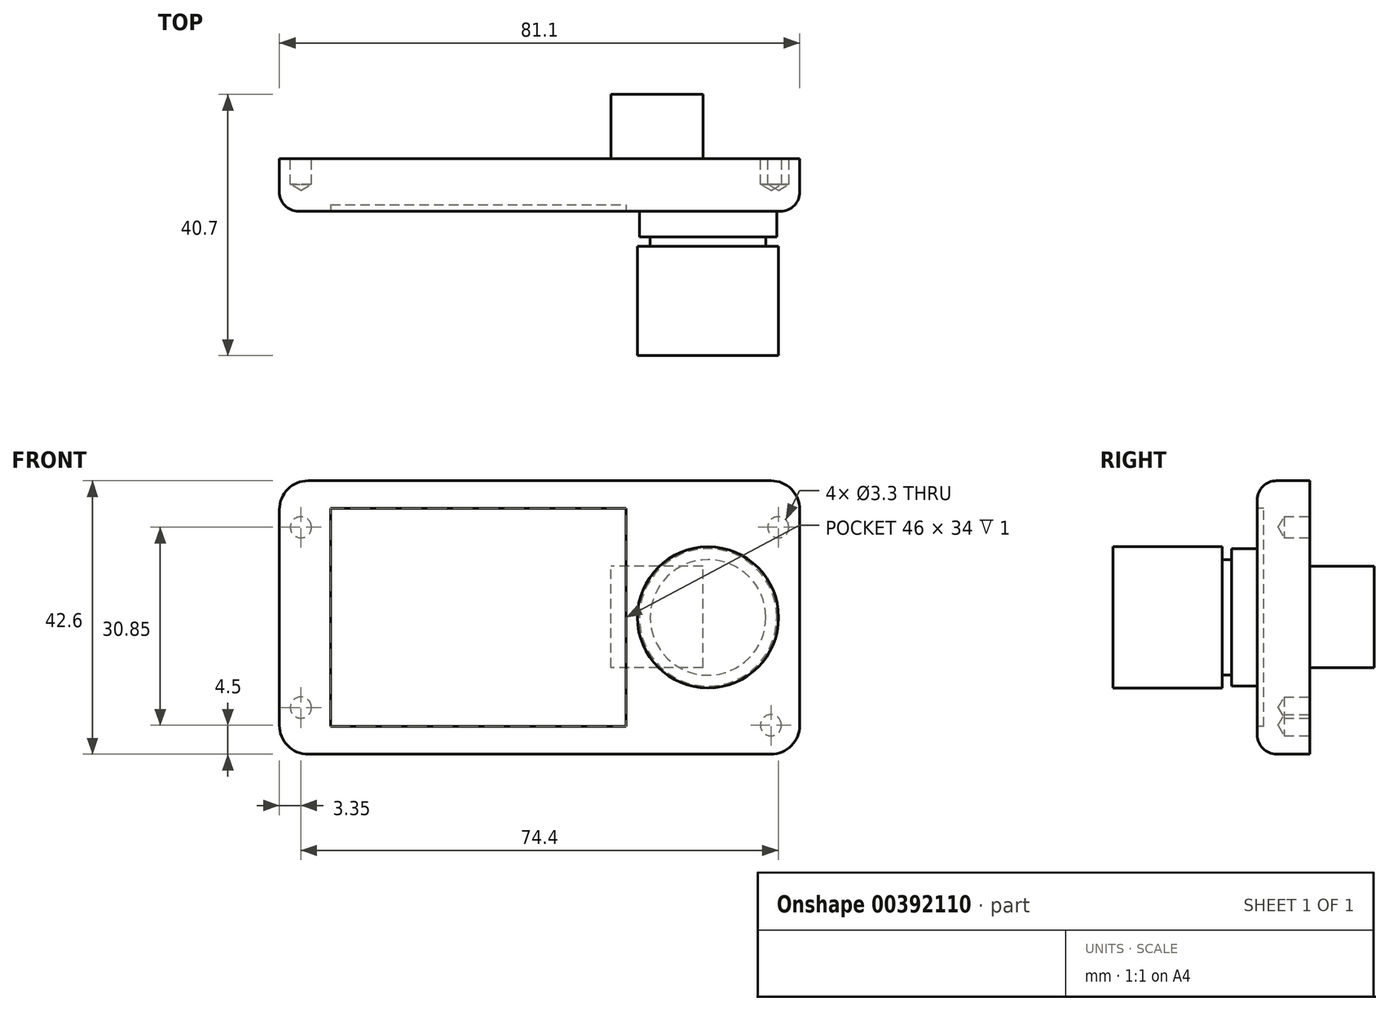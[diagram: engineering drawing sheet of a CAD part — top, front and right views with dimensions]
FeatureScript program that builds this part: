
annotation { "Feature Type Name" : "Feature", "Feature Type Description" : "" }
export const myFeature = defineFeature(function(context is Context, id is Id, definition is map)
    precondition{}
    {
        {
            var Q0;
            Q0=qCreatedBy(makeId("Front.planeOp"),FACE);
            var sketch = newSketch(context, id + "F0", { "sketchPlane" : qUnion([Q0])});
            skLineSegment(sketch, "E0.bottom", {"start": v(36.05, 21.3) * mm, "end": v(-36.05, 21.3) * mm});
            skLineSegment(sketch, "E0.top", {"start": v(36.05, -21.3) * mm, "end": v(-36.05, -21.3) * mm});
            skLineSegment(sketch, "E0.left", {"start": v(40.55, 16.8) * mm, "end": v(40.55, -16.8) * mm});
            skLineSegment(sketch, "E0.right", {"start": v(-40.55, 16.8) * mm, "end": v(-40.55, -16.8) * mm});
            skPoint(sketch, "E0.middle", {"position": v(0, 0) * mm});
            skArc(sketch, "E1.filletArc", {"start": v(-36.05, 21.3) * mm, "mid": v(-39.23, 19.98) * mm, "end": v(-40.55, 16.8) * mm});
            skPoint(sketch, "E2.visualSharp", {"position": v(40.55, 21.3) * mm});
            skArc(sketch, "E2.filletArc", {"start": v(40.55, 16.8) * mm, "mid": v(39.23, 19.98) * mm, "end": v(36.05, 21.3) * mm});
            skPoint(sketch, "E3.visualSharp", {"position": v(40.55, -21.3) * mm});
            skArc(sketch, "E3.filletArc", {"start": v(36.05, -21.3) * mm, "mid": v(39.23, -19.98) * mm, "end": v(40.55, -16.8) * mm});
            skPoint(sketch, "E4.visualSharp", {"position": v(-40.55, -21.3) * mm});
            skArc(sketch, "E4.filletArc", {"start": v(-40.55, -16.8) * mm, "mid": v(-39.23, -19.98) * mm, "end": v(-36.05, -21.3) * mm});
            skLineSegment(sketch, "E5", {"start": v(40.55, 0) * mm, "end": v(-40.55, 0) * mm, "construction": true});
            skLineSegment(sketch, "E6", {"start": v(0, 21.3) * mm, "end": v(0, -21.3) * mm, "construction": true});
            skLineSegment(sketch, "E7.bottom", {"start": v(-37.2, 14.05) * mm, "end": v(37.2, 14.05) * mm, "construction": true});
            skLineSegment(sketch, "E7.top", {"start": v(-37.2, -14.05) * mm, "end": v(37.2, -14.05) * mm, "construction": true});
            skLineSegment(sketch, "E7.left", {"start": v(-37.2, 14.05) * mm, "end": v(-37.2, -14.05) * mm, "construction": true});
            skLineSegment(sketch, "E7.right", {"start": v(37.2, 14.05) * mm, "end": v(37.2, -14.05) * mm, "construction": true});
            skPoint(sketch, "E8", {"position": v(37.2, 14.05) * mm});
            skPoint(sketch, "E9", {"position": v(37.2, -14.05) * mm});
            skPoint(sketch, "E10", {"position": v(-37.2, -14.05) * mm});
            skPoint(sketch, "E11", {"position": v(-37.2, 14.05) * mm});
            skSolve(sketch);
        }
        {
            var Q0;
            Q0=makeQuery(id+"F0.imprint","IMPRINT",FACE,{"disambiguationData":[TD([[makeQuery(id+"F0.imprint","IMPRINT",EDGE,{"derivedFrom":sQuery(id+"F0.wireOp",EDGE,"E0.bottom")}),1.0]])]});
            extrude(context, id + "F1", {"entities" : qUnion([Q0]), "depth" : 8.2 * mm});
        }
        {
            var Q0;
            Q0=makeQuery(id+"F1.opExtrude","CAP_FACE",FACE,{"disambiguationData":[OSD([sQuery(id+"F0.wireOp",EDGE,"E0.bottom"),sQuery(id+"F0.wireOp",EDGE,"E0.top"),sQuery(id+"F0.wireOp",EDGE,"E0.left"),sQuery(id+"F0.wireOp",EDGE,"E0.right"),sQuery(id+"F0.wireOp",EDGE,"E1.filletArc"),sQuery(id+"F0.wireOp",EDGE,"E2.filletArc"),sQuery(id+"F0.wireOp",EDGE,"E3.filletArc"),sQuery(id+"F0.wireOp",EDGE,"E4.filletArc")])],"isStart":true});
            var sketch = newSketch(context, id + "F2", { "sketchPlane" : qUnion([Q0])});
            skLineSegment(sketch, "E12.bottom", {"start": v(-25.45, -7.8) * mm, "end": v(-11.15, -7.8) * mm});
            skLineSegment(sketch, "E12.top", {"start": v(-25.45, 8) * mm, "end": v(-11.15, 8) * mm});
            skLineSegment(sketch, "E12.left", {"start": v(-25.45, -7.8) * mm, "end": v(-25.45, 8) * mm});
            skLineSegment(sketch, "E12.right", {"start": v(-11.15, -7.8) * mm, "end": v(-11.15, 8) * mm});
            skSolve(sketch);
        }
        {
            var Q0;
            Q0=makeQuery(id+"F2.imprint","IMPRINT",FACE,{"disambiguationData":[TD([[makeQuery(id+"F2.imprint","IMPRINT",EDGE,{"derivedFrom":sQuery(id+"F2.wireOp",EDGE,"E12.bottom")}),1.0]])]});
            extrude(context, id + "F3", {"entities" : qUnion([Q0]), "operationType" : NewBodyOperationType.ADD, "depth" : 10 * mm});
        }
        {
            var Q0;
            Q0=makeQuery(id+"F1.opExtrude","CAP_FACE",FACE,{"disambiguationData":[OSD([sQuery(id+"F0.wireOp",EDGE,"E0.bottom"),sQuery(id+"F0.wireOp",EDGE,"E0.top"),sQuery(id+"F0.wireOp",EDGE,"E0.left"),sQuery(id+"F0.wireOp",EDGE,"E0.right"),sQuery(id+"F0.wireOp",EDGE,"E1.filletArc"),sQuery(id+"F0.wireOp",EDGE,"E2.filletArc"),sQuery(id+"F0.wireOp",EDGE,"E3.filletArc"),sQuery(id+"F0.wireOp",EDGE,"E4.filletArc")])],"isStart":false});
            var sketch = newSketch(context, id + "F4", { "sketchPlane" : qUnion([Q0])});
            skCircle(sketch, "E13", {"center": v(26.25, 0) * mm, "radius": 10.7 * mm});
            skSolve(sketch);
        }
        {
            var Q0;
            Q0=makeQuery(id+"F4.imprint","IMPRINT",FACE,{"disambiguationData":[TD([[makeQuery(id+"F4.imprint","IMPRINT",EDGE,{"derivedFrom":sQuery(id+"F4.wireOp",EDGE,"E13")}),1.0]])]});
            extrude(context, id + "F5", {"entities" : qUnion([Q0]), "operationType" : NewBodyOperationType.ADD, "depth" : 4 * mm});
        }
        {
            var Q0;
            Q0=makeQuery(id+"F4.imprint","IMPRINT",FACE,{"disambiguationData":[TD([[makeQuery(id+"F4.imprint","IMPRINT",EDGE,{"derivedFrom":sQuery(id+"F4.wireOp",EDGE,"E13")}),-1.0]])]});
            var sketch = newSketch(context, id + "F6", { "sketchPlane" : qUnion([Q0])});
            skLineSegment(sketch, "E14.bottom", {"start": v(-32.55, -17) * mm, "end": v(13.45, -17) * mm});
            skLineSegment(sketch, "E14.top", {"start": v(-32.55, 17) * mm, "end": v(13.45, 17) * mm});
            skLineSegment(sketch, "E14.left", {"start": v(-32.55, -17) * mm, "end": v(-32.55, 17) * mm});
            skLineSegment(sketch, "E14.right", {"start": v(13.45, -17) * mm, "end": v(13.45, 17) * mm});
            skLineSegment(sketch, "E15", {"start": v(0, 0) * mm, "end": v(-40.5, 0) * mm});
            skPoint(sketch, "E15.endSnap0", {"position": v(-32.55, 0) * mm});
            skSolve(sketch);
        }
        {
            var Q0;
            {var subQ3=sQuery(id+"F6.wireOp",EDGE,"E14.bottom");Q0=makeQuery(id+"F6.imprint","IMPRINT",FACE,{"disambiguationData":[TD([[makeQuery(id+"F6.imprint","IMPRINT",EDGE,{"derivedFrom":subQ3}),1.0]])]});}
            extrude(context, id + "F7", {"entities" : qUnion([Q0]), "operationType" : NewBodyOperationType.REMOVE, "oppositeDirection" : true, "depth" : 1 * mm});
        }
        {
            var Q0;
            Q0=makeQuery(id+"F1.opExtrude","CAP_EDGE",EDGE,{"disambiguationData":[OSD([sQuery(id+"F0.wireOp",EDGE,"E0.right")])],"isStart":false});
            var Q1;
            Q1=makeQuery(id+"F1.opExtrude","CAP_EDGE",EDGE,{"disambiguationData":[OSD([sQuery(id+"F0.wireOp",EDGE,"E4.filletArc")])],"isStart":false});
            var Q2;
            Q2=makeQuery(id+"F1.opExtrude","CAP_EDGE",EDGE,{"disambiguationData":[OSD([sQuery(id+"F0.wireOp",EDGE,"E0.left")])],"isStart":false});
            fillet(context, id + "F8", {"entities" : qUnion([Q0, Q1, Q2]), "radius" : 3 * mm, "tangentPropagation" : true, "allowEdgeOverflow" : false});
        }
        {
            var Q0;
            Q0=sQuery(id+"F0.wireOp",VERTEX,"E8");
            var Q1;
            Q1=sQuery(id+"F0.wireOp",VERTEX,"E3.filletArc.center");
            var Q2;
            Q2=sQuery(id+"F0.wireOp",VERTEX,"E10");
            var Q3;
            Q3=sQuery(id+"F0.wireOp",VERTEX,"E11");
            var Q4;
            Q4=makeQuery(id+"F1.opExtrude","SWEPT_BODY",BODY,{"disambiguationData":[OSD([sQuery(id+"F0.wireOp",EDGE,"E0.bottom"),sQuery(id+"F0.wireOp",EDGE,"E0.top"),sQuery(id+"F0.wireOp",EDGE,"E0.left"),sQuery(id+"F0.wireOp",EDGE,"E0.right"),sQuery(id+"F0.wireOp",EDGE,"E1.filletArc"),sQuery(id+"F0.wireOp",EDGE,"E2.filletArc"),sQuery(id+"F0.wireOp",EDGE,"E3.filletArc"),sQuery(id+"F0.wireOp",EDGE,"E4.filletArc")])]});
            hole(context, id + "F9", {"style" : HoleStyle.SIMPLE, "endStyle" : HoleEndStyle.BLIND, "oppositeDirection" : true, "standardTappedOrClearance" : lookupTablePath({ "standard" : "ISO", "fit" : "Normal", "size" : "M3", "type" : "Clearance" }), "standardBlindInLast" : lookupTablePath({ "fit" : "Standard", "standard" : "ISO", "size" : "M3", "type" : "Clearance" }), "holeDiameter" : 3.3 * mm, "holeDepth" : 4 * mm, "isTappedThrough" : true, "tappedDepth" : 4 * mm, "tapClearance" : 0, "locations" : qUnion([Q0, Q1, Q2, Q3]), "scope" : qUnion([Q4])});
        }
        {
            var Q0;
            Q0=makeQuery(id+"F5.opExtrude","CAP_FACE",FACE,{"disambiguationData":[OSD([sQuery(id+"F4.wireOp",EDGE,"E13")])],"isStart":false});
            var sketch = newSketch(context, id + "F10", { "sketchPlane" : qUnion([Q0])});
            skCircle(sketch, "E16", {"center": v(26.25, 0) * mm, "radius": 9 * mm});
            skSolve(sketch);
        }
        {
            var Q0;
            Q0=makeQuery(id+"F10.imprint","IMPRINT",FACE,{"disambiguationData":[TD([[makeQuery(id+"F10.imprint","IMPRINT",EDGE,{"derivedFrom":sQuery(id+"F10.wireOp",EDGE,"E16")}),1.0]])]});
            extrude(context, id + "F11", {"entities" : qUnion([Q0]), "operationType" : NewBodyOperationType.ADD, "depth" : 1.5 * mm});
        }
        {
            var Q0;
            Q0=makeQuery(id+"F11.opExtrude","CAP_FACE",FACE,{"disambiguationData":[OSD([sQuery(id+"F10.wireOp",EDGE,"E16")])],"isStart":false});
            var sketch = newSketch(context, id + "F12", { "sketchPlane" : qUnion([Q0])});
            skCircle(sketch, "E17", {"center": v(26.25, 0) * mm, "radius": 11 * mm});
            skSolve(sketch);
        }
        {
            var Q0;
            Q0=makeQuery(id+"F12.imprint","IMPRINT",FACE,{"disambiguationData":[TD([[makeQuery(id+"F12.imprint","IMPRINT",EDGE,{"derivedFrom":makeQuery(id+"F11.opExtrude","CAP_EDGE",EDGE,{"disambiguationData":[OSD([sQuery(id+"F10.wireOp",EDGE,"E16")])],"isStart":false})}),1.0]])]});
            var Q1;
            Q1=makeQuery(id+"F12.imprint","IMPRINT",FACE,{"disambiguationData":[TD([[makeQuery(id+"F12.imprint","IMPRINT",EDGE,{"derivedFrom":sQuery(id+"F12.wireOp",EDGE,"E17")}),1.0]])]});
            extrude(context, id + "F13", {"entities" : qUnion([Q0, Q1]), "operationType" : NewBodyOperationType.ADD, "depth" : 17 * mm});
        }
    });
